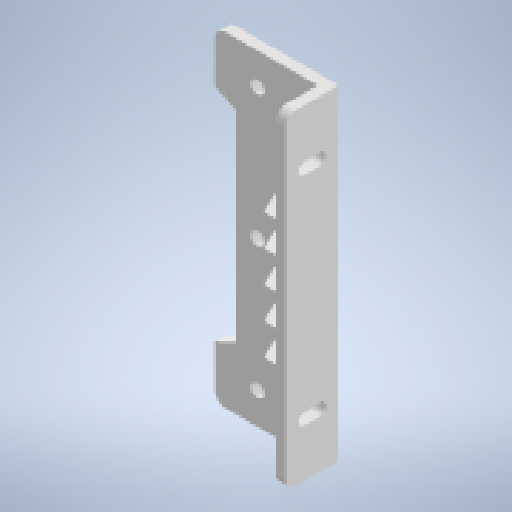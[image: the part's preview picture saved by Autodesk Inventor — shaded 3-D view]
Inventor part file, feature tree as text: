
AUTODESK INVENTOR PART (.ipt)
format: ipt  version: 2023 (Build 270158000, 158)  size: 280,064 bytes
history: native  units: mm
features: extrude x6, sketch x6, reference x5, other x4, projected_geometry x3, shell x1, mirror x1, draft x1, pattern_linear x1, fillet x1
ambient origin geometry x8: Origin, YZ Plane, XZ Plane, XY Plane, X Axis, Y Axis, Z Axis, Center Point
bodies: Solid1 (feature_tree)
feature tree (29):
  extrude  "Extrusion1"  Depth=6.0mm
  shell  "Shell1"  Thickness=8.0mm
  extrude  "Extrusion2"  Depth=2.0mm
  extrude  "Extrusion3"  Depth=2.25mm
  extrude  "Extrusion4"  TaperAngle=0.0deg  [1 undecoded]
  extrude  "Extrusion5"  TaperAngle=0.0deg  [1 undecoded]
  mirror  "Mirror1"
  extrude  "Extrusion6"  Depth=2.0mm
  draft  "FaceDraft1"
  pattern_linear  "Rectangular Pattern1"  Spacing1=11.34464mm  [1 undecoded]
  fillet  "Fillet1"  Radius=2.5mm
  sketch  "Sketch1"  dims[d0=6.0mm d1=6.0mm d2=8.0mm]
  reference  "Reference1"
  reference  "Reference2"
  sketch  "Sketch2"  dims[d3=10.0mm d4=0.0mm d5=2.0mm]
  reference  "Reference3"
  reference  "Reference4"
  projected_geometry  "Projected Loop1"
  sketch  "Sketch3"  dims[d6=1.5mm d7=2.25mm]
  reference  "Reference5"
  sketch  "Sketch4"  dims[d8=1.5mm d9=0.0mm]
  sketch  "Sketch5"  dims[d10=2.25mm d11=0.0mm d12=0.0mm]
  projected_geometry  "Projected Loop2"
  sketch  "Sketch7"  dims[d13=0.0mm d14=0.0mm d15=11.34464mm d16=11.34464mm d18=2.5mm d19=2.5mm d20=4.0mm d21=0.0mm d22=0.0mm d24=9.428595mm d25=10.0mm d26=11.34464mm d27=11.34464mm d28=10.0mm d29=4.0mm d30=0.0mm d31=0.0mm d32=1.0mm d33=1.0mm d34=6.0mm d35=0.0mm d36=4.363323mm d37=50.0mm d39=6.0mm d40=2.0mm]
  projected_geometry  "Projected Loop4"
  parser-record x1  (decoder bookkeeping rows leaked as tree rows — omitted from the tree; the rows remain in map.json)
  other  "A.iam"
  other  "A-06:1"
  other  "A-03:1"
note: 3 required parameter values undecoded (feature->parameter linkage not recoverable at this tier; creation-order binding heuristic only, values carry confidence <= 0.55)
note: 1 file-system path scrubbed to <path> (originals preserved in map.json)
